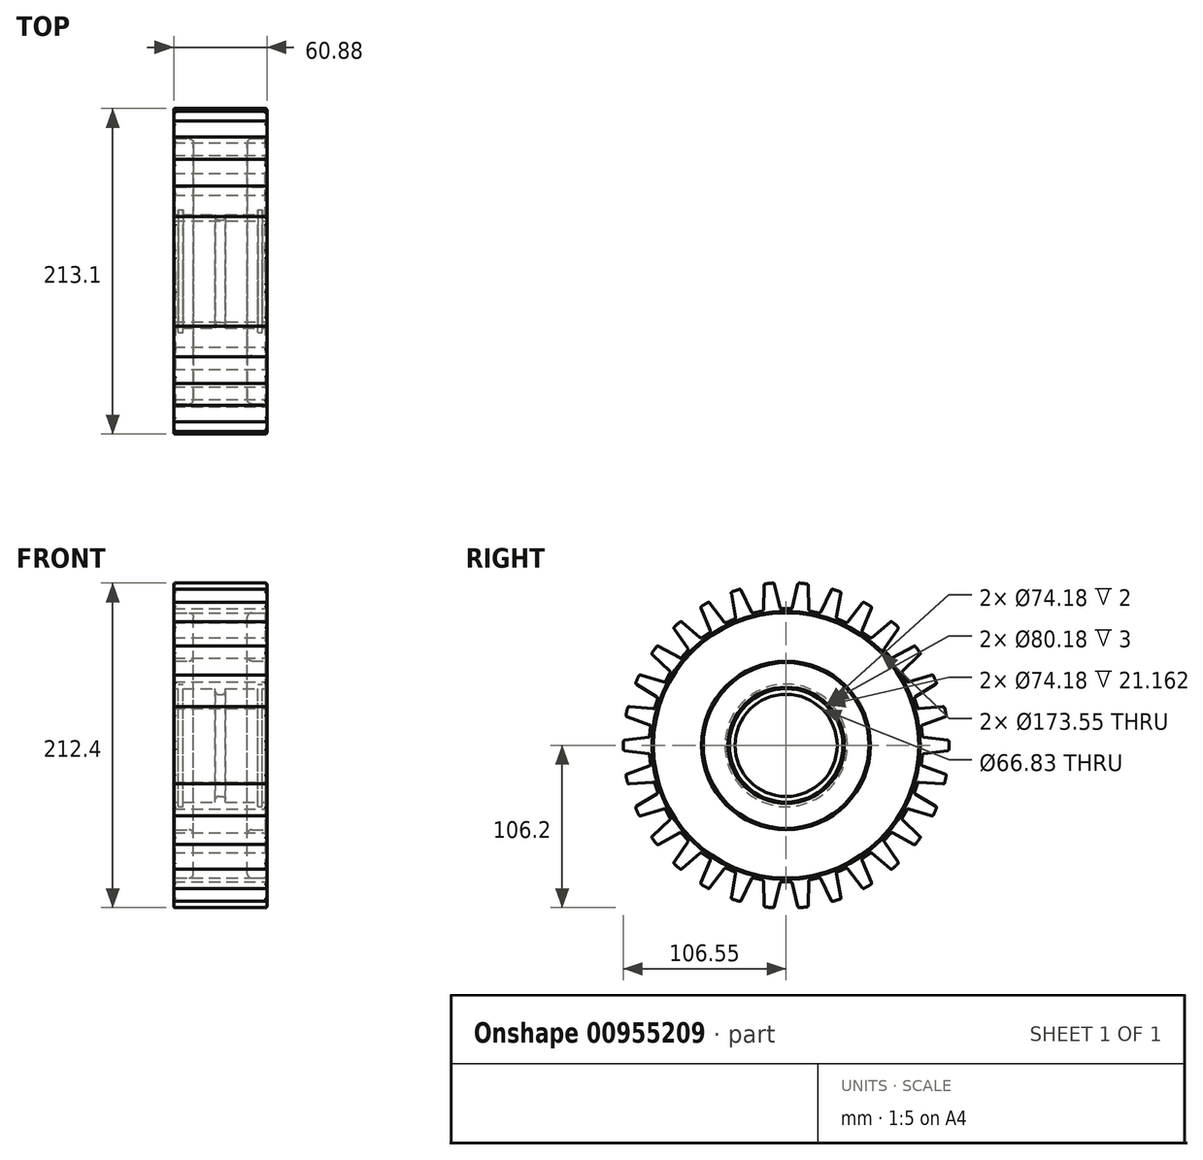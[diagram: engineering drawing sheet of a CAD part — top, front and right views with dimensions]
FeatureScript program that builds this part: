
annotation { "Feature Type Name" : "Feature", "Feature Type Description" : "" }
export const myFeature = defineFeature(function(context is Context, id is Id, definition is map)
    precondition{}
    {
        {
            var Q0;
            Q0=qCreatedBy(makeId("Front.planeOp"),FACE);
            var sketch = newSketch(context, id + "F0", { "sketchPlane" : qUnion([Q0])});
            skLineSegment(sketch, "E0", {"start": v(0, 106.55) * mm, "end": v(-30.44, 106.55) * mm});
            skLineSegment(sketch, "E1", {"start": v(-30.44, 106.55) * mm, "end": v(-30.44, 86.78) * mm});
            skLineSegment(sketch, "E2", {"start": v(-30.44, 37.1) * mm, "end": v(-27.44, 37.1) * mm});
            skLineSegment(sketch, "E3", {"start": v(-27.44, 37.1) * mm, "end": v(-27.44, 40.1) * mm});
            skLineSegment(sketch, "E4", {"start": v(-27.44, 40.1) * mm, "end": v(-24.44, 40.1) * mm});
            skLineSegment(sketch, "E5", {"start": v(-24.44, 40.1) * mm, "end": v(-24.44, 37.1) * mm});
            skLineSegment(sketch, "E6", {"start": v(-24.44, 37.1) * mm, "end": v(-3.28, 37.1) * mm});
            skLineSegment(sketch, "E7", {"start": v(-3.28, 37.1) * mm, "end": v(-3.28, 33.41) * mm});
            skLineSegment(sketch, "E8", {"start": v(-3.28, 33.41) * mm, "end": v(0, 33.41) * mm});
            skLineSegment(sketch, "E9", {"start": v(-30.44, 55.2) * mm, "end": v(-20.58, 55.2) * mm});
            skLineSegment(sketch, "E10", {"start": v(-17.58, 58.2) * mm, "end": v(-17.58, 83.78) * mm});
            skLineSegment(sketch, "E11", {"start": v(-20.58, 86.78) * mm, "end": v(-30.44, 86.78) * mm});
            skLineSegment(sketch, "E12.trimOffspring", {"start": v(-30.44, 55.2) * mm, "end": v(-30.44, 37.1) * mm});
            skPoint(sketch, "E13.visualSharp", {"position": v(-17.58, 86.78) * mm});
            skArc(sketch, "E13.filletArc", {"start": v(-17.58, 83.78) * mm, "mid": v(-18.46, 85.9) * mm, "end": v(-20.58, 86.78) * mm});
            skPoint(sketch, "E14.visualSharp", {"position": v(-17.58, 55.2) * mm});
            skArc(sketch, "E14.filletArc", {"start": v(-20.58, 55.2) * mm, "mid": v(-18.46, 56.08) * mm, "end": v(-17.58, 58.2) * mm});
            skLineSegment(sketch, "E15.MirrorCS", {"start": v(0, 106.55) * mm, "end": v(30.44, 106.55) * mm});
            skLineSegment(sketch, "E16.MirrorCS", {"start": v(30.44, 106.55) * mm, "end": v(30.44, 86.78) * mm});
            skLineSegment(sketch, "E17.MirrorCS", {"start": v(20.58, 86.78) * mm, "end": v(30.44, 86.78) * mm});
            skArc(sketch, "E18.MirrorCS", {"start": v(17.58, 83.78) * mm, "mid": v(18.46, 85.9) * mm, "end": v(20.58, 86.78) * mm});
            skLineSegment(sketch, "E19.MirrorCS", {"start": v(17.58, 58.2) * mm, "end": v(17.58, 83.78) * mm});
            skArc(sketch, "E20.MirrorCS", {"start": v(20.58, 55.2) * mm, "mid": v(18.46, 56.08) * mm, "end": v(17.58, 58.2) * mm});
            skLineSegment(sketch, "E21.MirrorCS", {"start": v(30.44, 55.2) * mm, "end": v(20.58, 55.2) * mm});
            skLineSegment(sketch, "E22.MirrorCS", {"start": v(30.44, 55.2) * mm, "end": v(30.44, 37.1) * mm});
            skLineSegment(sketch, "E23.MirrorCS", {"start": v(30.44, 37.1) * mm, "end": v(27.44, 37.1) * mm});
            skLineSegment(sketch, "E24.MirrorCS", {"start": v(27.44, 40.1) * mm, "end": v(24.44, 40.1) * mm});
            skLineSegment(sketch, "E25.MirrorCS", {"start": v(24.44, 40.1) * mm, "end": v(24.44, 37.1) * mm});
            skLineSegment(sketch, "E26.MirrorCS", {"start": v(24.44, 37.1) * mm, "end": v(3.28, 37.1) * mm});
            skLineSegment(sketch, "E27.MirrorCS", {"start": v(3.28, 37.1) * mm, "end": v(3.28, 33.41) * mm});
            skLineSegment(sketch, "E28.MirrorCS", {"start": v(3.28, 33.41) * mm, "end": v(0, 33.41) * mm});
            skLineSegment(sketch, "E29.MirrorCS", {"start": v(27.44, 37.1) * mm, "end": v(27.44, 40.1) * mm});
            skLineSegment(sketch, "E30", {"start": v(0, 0) * mm, "end": v(-35.69, 0) * mm, "construction": true});
            skSolve(sketch);
        }
        {
            var Q0;
            Q0=makeQuery(id+"F0.imprint","IMPRINT",FACE,{"disambiguationData":[TD([[makeQuery(id+"F0.imprint","IMPRINT",EDGE,{"derivedFrom":sQuery(id+"F0.wireOp",EDGE,"E0")}),1.0]])]});
            var Q1;
            Q1=sQuery(id+"F0.wireOp",EDGE,"E30");
            revolve(context, id + "F1", {"surfaceOperationType" : NewSurfaceOperationType.NEW, "entities" : qUnion([Q0]), "axis" : qUnion([Q1]), "revolveType" : RevolveType.FULL});
        }
        {
            var Q0;
            Q0=qCreatedBy(makeId("Right.planeOp"),FACE);
            var sketch = newSketch(context, id + "F2", { "sketchPlane" : qUnion([Q0])});
            skLineSegment(sketch, "E31", {"start": v(0, 0) * mm, "end": v(0, 103.53) * mm});
            skLineSegment(sketch, "E32", {"start": v(4.04, 90.14) * mm, "end": v(8.11, 107.16) * mm});
            skLineSegment(sketch, "E33.MirrorCS", {"start": v(-4.04, 90.14) * mm, "end": v(-8.11, 107.16) * mm});
            skLineSegment(sketch, "E34", {"start": v(-3.06, 89.37) * mm, "end": v(3.06, 89.37) * mm});
            skLineSegment(sketch, "E35", {"start": v(8.11, 107.16) * mm, "end": v(-8.11, 107.16) * mm});
            skPoint(sketch, "E36.visualSharp", {"position": v(-3.85, 89.37) * mm});
            skArc(sketch, "E36.filletArc", {"start": v(-4.04, 90.14) * mm, "mid": v(-3.68, 89.58) * mm, "end": v(-3.06, 89.37) * mm});
            skPoint(sketch, "E37.visualSharp", {"position": v(3.85, 89.37) * mm});
            skArc(sketch, "E37.filletArc", {"start": v(3.06, 89.37) * mm, "mid": v(3.68, 89.58) * mm, "end": v(4.04, 90.14) * mm});
            skSolve(sketch);
        }
        {
            var Q0;
            Q0=makeQuery(id+"F2.imprint","IMPRINT",FACE,{"disambiguationData":[TD([[makeQuery(id+"F2.imprint","IMPRINT",EDGE,{"derivedFrom":sQuery(id+"F2.wireOp",EDGE,"E32")}),1.0]])]});
            extrude(context, id + "F3", {"entities" : qUnion([Q0]), "operationType" : NewBodyOperationType.REMOVE, "endBound" : BoundingType.SYMMETRIC, "oppositeDirection" : true, "depth" : 70 * mm, "offsetDistance" : 25 * mm});
        }
        {
            var Q0;
            Q0=makeQuery(id+"F3.boolean.opBoolean","COPY",FACE,{"derivedFrom":makeQuery(id+"F3.opExtrude","SWEPT_FACE",FACE,{"disambiguationData":[OSD([sQuery(id+"F2.wireOp",EDGE,"E32")])]})});
            var Q1;
            Q1=makeQuery(id+"F3.boolean.opBoolean","COPY",FACE,{"derivedFrom":makeQuery(id+"F3.opExtrude","SWEPT_FACE",FACE,{"disambiguationData":[OSD([sQuery(id+"F2.wireOp",EDGE,"E37.filletArc")])]})});
            var Q2;
            Q2=makeQuery(id+"F3.boolean.opBoolean","COPY",FACE,{"derivedFrom":makeQuery(id+"F3.opExtrude","SWEPT_FACE",FACE,{"disambiguationData":[OSD([sQuery(id+"F2.wireOp",EDGE,"E34")])]})});
            var Q3;
            Q3=makeQuery(id+"F3.boolean.opBoolean","COPY",FACE,{"derivedFrom":makeQuery(id+"F3.opExtrude","SWEPT_FACE",FACE,{"disambiguationData":[OSD([sQuery(id+"F2.wireOp",EDGE,"E36.filletArc")])]})});
            var Q4;
            Q4=makeQuery(id+"F3.boolean.opBoolean","COPY",FACE,{"derivedFrom":makeQuery(id+"F3.opExtrude","SWEPT_FACE",FACE,{"disambiguationData":[OSD([sQuery(id+"F2.wireOp",EDGE,"E33.MirrorCS")])]})});
            var Q5;
            Q5=sQuery(id+"F0.wireOp",EDGE,"E30");
            circularPattern(context, id + "F4", {"patternType" : PatternType.FACE, "faces" : qUnion([Q0, Q1, Q2, Q3, Q4]), "axis" : qUnion([Q5]), "angle" : 360 * degree, "instanceCount" : 30, "equalSpace" : true});
        }
        {
            var Q0;
            Q0=makeQuery(id+"F1.opRevolve","SWEPT_EDGE",EDGE,{"disambiguationData":[OSD([sQuery(id+"F0.wireOp",EDGE,"E1"),sQuery(id+"F0.wireOp",EDGE,"E11")])]});
            var Q1;
            Q1=makeQuery(id+"F1.opRevolve","SWEPT_EDGE",EDGE,{"disambiguationData":[OSD([sQuery(id+"F0.wireOp",EDGE,"E9"),sQuery(id+"F0.wireOp",EDGE,"E12.trimOffspring")])]});
            var Q2;
            Q2=makeQuery(id+"F1.opRevolve","SWEPT_EDGE",EDGE,{"disambiguationData":[OSD([sQuery(id+"F0.wireOp",EDGE,"E2"),sQuery(id+"F0.wireOp",EDGE,"E12.trimOffspring")])]});
            var Q3;
            Q3=makeQuery(id+"F1.opRevolve","SWEPT_EDGE",EDGE,{"disambiguationData":[OSD([sQuery(id+"F0.wireOp",EDGE,"E16.MirrorCS"),sQuery(id+"F0.wireOp",EDGE,"E17.MirrorCS")])]});
            var Q4;
            Q4=makeQuery(id+"F1.opRevolve","SWEPT_EDGE",EDGE,{"disambiguationData":[OSD([sQuery(id+"F0.wireOp",EDGE,"E21.MirrorCS"),sQuery(id+"F0.wireOp",EDGE,"E22.MirrorCS")])]});
            var Q5;
            Q5=makeQuery(id+"F1.opRevolve","SWEPT_EDGE",EDGE,{"disambiguationData":[OSD([sQuery(id+"F0.wireOp",EDGE,"E22.MirrorCS"),sQuery(id+"F0.wireOp",EDGE,"E23.MirrorCS")])]});
            chamfer(context, id + "F5", {"entities" : qUnion([Q0, Q1, Q2, Q3, Q4, Q5]), "width" : 1 * mm, "tangentPropagation" : true});
        }
        {
            var Q0;
            Q0=makeQuery(id+"F4.opPattern","COPY",EDGE,{"derivedFrom":makeQuery(id+"F3.boolean.opBoolean","INTERSECT",EDGE,{"derivedFrom":[makeQuery(id+"F1.opRevolve","SWEPT_FACE",FACE,{"disambiguationData":[OSD([sQuery(id+"F0.wireOp",EDGE,"E0"),sQuery(id+"F0.wireOp",EDGE,"E15.MirrorCS")])]}),makeQuery(id+"F3.opExtrude","SWEPT_FACE",FACE,{"disambiguationData":[OSD([sQuery(id+"F2.wireOp",EDGE,"E33.MirrorCS")])]})]}),"instanceName":"3"});
            var Q1;
            Q1=makeQuery(id+"F4.opPattern","COPY",EDGE,{"derivedFrom":makeQuery(id+"F3.boolean.opBoolean","INTERSECT",EDGE,{"derivedFrom":[makeQuery(id+"F1.opRevolve","SWEPT_FACE",FACE,{"disambiguationData":[OSD([sQuery(id+"F0.wireOp",EDGE,"E0"),sQuery(id+"F0.wireOp",EDGE,"E15.MirrorCS")])]}),makeQuery(id+"F3.opExtrude","SWEPT_FACE",FACE,{"disambiguationData":[OSD([sQuery(id+"F2.wireOp",EDGE,"E32")])]})]}),"instanceName":"2"});
            var Q2;
            Q2=makeQuery(id+"F4.opPattern","COPY",EDGE,{"derivedFrom":makeQuery(id+"F3.boolean.opBoolean","INTERSECT",EDGE,{"derivedFrom":[makeQuery(id+"F1.opRevolve","SWEPT_FACE",FACE,{"disambiguationData":[OSD([sQuery(id+"F0.wireOp",EDGE,"E0"),sQuery(id+"F0.wireOp",EDGE,"E15.MirrorCS")])]}),makeQuery(id+"F3.opExtrude","SWEPT_FACE",FACE,{"disambiguationData":[OSD([sQuery(id+"F2.wireOp",EDGE,"E32")])]})]}),"instanceName":"3"});
            var Q3;
            Q3=makeQuery(id+"F4.opPattern","SPLIT",EDGE,{"disambiguationData":[OD(3.0)],"derivedFrom":makeQuery(id+"F1.opRevolve","SWEPT_EDGE",EDGE,{"disambiguationData":[OSD([sQuery(id+"F0.wireOp",EDGE,"E0"),sQuery(id+"F0.wireOp",EDGE,"E1")])]})});
            var Q4;
            Q4=makeQuery(id+"F4.opPattern","SPLIT",EDGE,{"disambiguationData":[OD(3.0)],"derivedFrom":makeQuery(id+"F1.opRevolve","SWEPT_EDGE",EDGE,{"disambiguationData":[OSD([sQuery(id+"F0.wireOp",EDGE,"E15.MirrorCS"),sQuery(id+"F0.wireOp",EDGE,"E16.MirrorCS")])]})});
            var Q5;
            Q5=makeQuery(id+"F4.opPattern","SPLIT",EDGE,{"disambiguationData":[OD(4.0)],"derivedFrom":makeQuery(id+"F1.opRevolve","SWEPT_EDGE",EDGE,{"disambiguationData":[OSD([sQuery(id+"F0.wireOp",EDGE,"E0"),sQuery(id+"F0.wireOp",EDGE,"E1")])]})});
            var Q6;
            Q6=makeQuery(id+"F4.opPattern","SPLIT",EDGE,{"disambiguationData":[OD(4.0)],"derivedFrom":makeQuery(id+"F1.opRevolve","SWEPT_EDGE",EDGE,{"disambiguationData":[OSD([sQuery(id+"F0.wireOp",EDGE,"E15.MirrorCS"),sQuery(id+"F0.wireOp",EDGE,"E16.MirrorCS")])]})});
            var Q7;
            Q7=makeQuery(id+"F4.opPattern","COPY",EDGE,{"derivedFrom":makeQuery(id+"F3.boolean.opBoolean","INTERSECT",EDGE,{"derivedFrom":[makeQuery(id+"F1.opRevolve","SWEPT_FACE",FACE,{"disambiguationData":[OSD([sQuery(id+"F0.wireOp",EDGE,"E0"),sQuery(id+"F0.wireOp",EDGE,"E15.MirrorCS")])]}),makeQuery(id+"F3.opExtrude","SWEPT_FACE",FACE,{"disambiguationData":[OSD([sQuery(id+"F2.wireOp",EDGE,"E33.MirrorCS")])]})]}),"instanceName":"4"});
            var Q8;
            Q8=makeQuery(id+"F4.opPattern","SPLIT",EDGE,{"disambiguationData":[OD(5.0)],"derivedFrom":makeQuery(id+"F1.opRevolve","SWEPT_EDGE",EDGE,{"disambiguationData":[OSD([sQuery(id+"F0.wireOp",EDGE,"E0"),sQuery(id+"F0.wireOp",EDGE,"E1")])]})});
            var Q9;
            Q9=makeQuery(id+"F4.opPattern","COPY",EDGE,{"derivedFrom":makeQuery(id+"F3.boolean.opBoolean","INTERSECT",EDGE,{"derivedFrom":[makeQuery(id+"F1.opRevolve","SWEPT_FACE",FACE,{"disambiguationData":[OSD([sQuery(id+"F0.wireOp",EDGE,"E0"),sQuery(id+"F0.wireOp",EDGE,"E15.MirrorCS")])]}),makeQuery(id+"F3.opExtrude","SWEPT_FACE",FACE,{"disambiguationData":[OSD([sQuery(id+"F2.wireOp",EDGE,"E32")])]})]}),"instanceName":"4"});
            var Q10;
            Q10=makeQuery(id+"F4.opPattern","SPLIT",EDGE,{"disambiguationData":[OD(5.0)],"derivedFrom":makeQuery(id+"F1.opRevolve","SWEPT_EDGE",EDGE,{"disambiguationData":[OSD([sQuery(id+"F0.wireOp",EDGE,"E15.MirrorCS"),sQuery(id+"F0.wireOp",EDGE,"E16.MirrorCS")])]})});
            var Q11;
            Q11=makeQuery(id+"F4.opPattern","COPY",EDGE,{"derivedFrom":makeQuery(id+"F3.boolean.opBoolean","INTERSECT",EDGE,{"derivedFrom":[makeQuery(id+"F1.opRevolve","SWEPT_FACE",FACE,{"disambiguationData":[OSD([sQuery(id+"F0.wireOp",EDGE,"E0"),sQuery(id+"F0.wireOp",EDGE,"E15.MirrorCS")])]}),makeQuery(id+"F3.opExtrude","SWEPT_FACE",FACE,{"disambiguationData":[OSD([sQuery(id+"F2.wireOp",EDGE,"E33.MirrorCS")])]})]}),"instanceName":"5"});
            var Q12;
            Q12=makeQuery(id+"F4.opPattern","SPLIT",EDGE,{"disambiguationData":[OD(6.0)],"derivedFrom":makeQuery(id+"F1.opRevolve","SWEPT_EDGE",EDGE,{"disambiguationData":[OSD([sQuery(id+"F0.wireOp",EDGE,"E0"),sQuery(id+"F0.wireOp",EDGE,"E1")])]})});
            var Q13;
            Q13=makeQuery(id+"F4.opPattern","COPY",EDGE,{"derivedFrom":makeQuery(id+"F3.boolean.opBoolean","INTERSECT",EDGE,{"derivedFrom":[makeQuery(id+"F1.opRevolve","SWEPT_FACE",FACE,{"disambiguationData":[OSD([sQuery(id+"F0.wireOp",EDGE,"E0"),sQuery(id+"F0.wireOp",EDGE,"E15.MirrorCS")])]}),makeQuery(id+"F3.opExtrude","SWEPT_FACE",FACE,{"disambiguationData":[OSD([sQuery(id+"F2.wireOp",EDGE,"E32")])]})]}),"instanceName":"5"});
            var Q14;
            Q14=makeQuery(id+"F4.opPattern","SPLIT",FACE,{"disambiguationData":[OD(6.0)],"derivedFrom":makeQuery(id+"F1.opRevolve","SWEPT_FACE",FACE,{"disambiguationData":[OSD([sQuery(id+"F0.wireOp",EDGE,"E0"),sQuery(id+"F0.wireOp",EDGE,"E15.MirrorCS")])]})});
            var Q15;
            Q15=makeQuery(id+"F4.opPattern","SPLIT",FACE,{"disambiguationData":[OD(7.0)],"derivedFrom":makeQuery(id+"F1.opRevolve","SWEPT_FACE",FACE,{"disambiguationData":[OSD([sQuery(id+"F0.wireOp",EDGE,"E0"),sQuery(id+"F0.wireOp",EDGE,"E15.MirrorCS")])]})});
            var Q16;
            Q16=makeQuery(id+"F4.opPattern","SPLIT",FACE,{"disambiguationData":[OD(8.0)],"derivedFrom":makeQuery(id+"F1.opRevolve","SWEPT_FACE",FACE,{"disambiguationData":[OSD([sQuery(id+"F0.wireOp",EDGE,"E0"),sQuery(id+"F0.wireOp",EDGE,"E15.MirrorCS")])]})});
            var Q17;
            Q17=makeQuery(id+"F4.opPattern","SPLIT",FACE,{"disambiguationData":[OD(9.0)],"derivedFrom":makeQuery(id+"F1.opRevolve","SWEPT_FACE",FACE,{"disambiguationData":[OSD([sQuery(id+"F0.wireOp",EDGE,"E0"),sQuery(id+"F0.wireOp",EDGE,"E15.MirrorCS")])]})});
            var Q18;
            Q18=makeQuery(id+"F4.opPattern","SPLIT",FACE,{"disambiguationData":[OD(10.0)],"derivedFrom":makeQuery(id+"F1.opRevolve","SWEPT_FACE",FACE,{"disambiguationData":[OSD([sQuery(id+"F0.wireOp",EDGE,"E0"),sQuery(id+"F0.wireOp",EDGE,"E15.MirrorCS")])]})});
            var Q19;
            Q19=makeQuery(id+"F4.opPattern","SPLIT",FACE,{"disambiguationData":[OD(11.0)],"derivedFrom":makeQuery(id+"F1.opRevolve","SWEPT_FACE",FACE,{"disambiguationData":[OSD([sQuery(id+"F0.wireOp",EDGE,"E0"),sQuery(id+"F0.wireOp",EDGE,"E15.MirrorCS")])]})});
            var Q20;
            Q20=makeQuery(id+"F4.opPattern","SPLIT",FACE,{"disambiguationData":[OD(12.0)],"derivedFrom":makeQuery(id+"F1.opRevolve","SWEPT_FACE",FACE,{"disambiguationData":[OSD([sQuery(id+"F0.wireOp",EDGE,"E0"),sQuery(id+"F0.wireOp",EDGE,"E15.MirrorCS")])]})});
            var Q21;
            Q21=makeQuery(id+"F4.opPattern","SPLIT",FACE,{"disambiguationData":[OD(13.0)],"derivedFrom":makeQuery(id+"F1.opRevolve","SWEPT_FACE",FACE,{"disambiguationData":[OSD([sQuery(id+"F0.wireOp",EDGE,"E0"),sQuery(id+"F0.wireOp",EDGE,"E15.MirrorCS")])]})});
            var Q22;
            Q22=makeQuery(id+"F4.opPattern","SPLIT",FACE,{"disambiguationData":[OD(14.0)],"derivedFrom":makeQuery(id+"F1.opRevolve","SWEPT_FACE",FACE,{"disambiguationData":[OSD([sQuery(id+"F0.wireOp",EDGE,"E0"),sQuery(id+"F0.wireOp",EDGE,"E15.MirrorCS")])]})});
            var Q23;
            Q23=makeQuery(id+"F4.opPattern","SPLIT",FACE,{"disambiguationData":[OD(15.0)],"derivedFrom":makeQuery(id+"F1.opRevolve","SWEPT_FACE",FACE,{"disambiguationData":[OSD([sQuery(id+"F0.wireOp",EDGE,"E0"),sQuery(id+"F0.wireOp",EDGE,"E15.MirrorCS")])]})});
            var Q24;
            Q24=makeQuery(id+"F4.opPattern","SPLIT",FACE,{"disambiguationData":[OD(16.0)],"derivedFrom":makeQuery(id+"F1.opRevolve","SWEPT_FACE",FACE,{"disambiguationData":[OSD([sQuery(id+"F0.wireOp",EDGE,"E0"),sQuery(id+"F0.wireOp",EDGE,"E15.MirrorCS")])]})});
            var Q25;
            Q25=makeQuery(id+"F4.opPattern","SPLIT",FACE,{"disambiguationData":[OD(17.0)],"derivedFrom":makeQuery(id+"F1.opRevolve","SWEPT_FACE",FACE,{"disambiguationData":[OSD([sQuery(id+"F0.wireOp",EDGE,"E0"),sQuery(id+"F0.wireOp",EDGE,"E15.MirrorCS")])]})});
            var Q26;
            Q26=makeQuery(id+"F4.opPattern","SPLIT",FACE,{"disambiguationData":[OD(18.0)],"derivedFrom":makeQuery(id+"F1.opRevolve","SWEPT_FACE",FACE,{"disambiguationData":[OSD([sQuery(id+"F0.wireOp",EDGE,"E0"),sQuery(id+"F0.wireOp",EDGE,"E15.MirrorCS")])]})});
            var Q27;
            Q27=makeQuery(id+"F4.opPattern","SPLIT",FACE,{"disambiguationData":[OD(19.0)],"derivedFrom":makeQuery(id+"F1.opRevolve","SWEPT_FACE",FACE,{"disambiguationData":[OSD([sQuery(id+"F0.wireOp",EDGE,"E0"),sQuery(id+"F0.wireOp",EDGE,"E15.MirrorCS")])]})});
            var Q28;
            Q28=makeQuery(id+"F4.opPattern","SPLIT",FACE,{"disambiguationData":[OD(20.0)],"derivedFrom":makeQuery(id+"F1.opRevolve","SWEPT_FACE",FACE,{"disambiguationData":[OSD([sQuery(id+"F0.wireOp",EDGE,"E0"),sQuery(id+"F0.wireOp",EDGE,"E15.MirrorCS")])]})});
            var Q29;
            Q29=makeQuery(id+"F4.opPattern","SPLIT",FACE,{"disambiguationData":[OD(21.0)],"derivedFrom":makeQuery(id+"F1.opRevolve","SWEPT_FACE",FACE,{"disambiguationData":[OSD([sQuery(id+"F0.wireOp",EDGE,"E0"),sQuery(id+"F0.wireOp",EDGE,"E15.MirrorCS")])]})});
            var Q30;
            Q30=makeQuery(id+"F4.opPattern","SPLIT",FACE,{"disambiguationData":[OD(22.0)],"derivedFrom":makeQuery(id+"F1.opRevolve","SWEPT_FACE",FACE,{"disambiguationData":[OSD([sQuery(id+"F0.wireOp",EDGE,"E0"),sQuery(id+"F0.wireOp",EDGE,"E15.MirrorCS")])]})});
            var Q31;
            Q31=makeQuery(id+"F4.opPattern","SPLIT",FACE,{"disambiguationData":[OD(2.0)],"derivedFrom":makeQuery(id+"F1.opRevolve","SWEPT_FACE",FACE,{"disambiguationData":[OSD([sQuery(id+"F0.wireOp",EDGE,"E0"),sQuery(id+"F0.wireOp",EDGE,"E15.MirrorCS")])]})});
            var Q32;
            Q32=makeQuery(id+"F4.opPattern","SPLIT",FACE,{"disambiguationData":[OD(0.0)],"derivedFrom":makeQuery(id+"F1.opRevolve","SWEPT_FACE",FACE,{"disambiguationData":[OSD([sQuery(id+"F0.wireOp",EDGE,"E0"),sQuery(id+"F0.wireOp",EDGE,"E15.MirrorCS")])]})});
            var Q33;
            Q33=makeQuery(id+"F4.opPattern","SPLIT",FACE,{"disambiguationData":[OD(1.0)],"derivedFrom":makeQuery(id+"F1.opRevolve","SWEPT_FACE",FACE,{"disambiguationData":[OSD([sQuery(id+"F0.wireOp",EDGE,"E0"),sQuery(id+"F0.wireOp",EDGE,"E15.MirrorCS")])]})});
            var Q34;
            Q34=makeQuery(id+"F4.opPattern","SPLIT",FACE,{"disambiguationData":[OD(29.0)],"derivedFrom":makeQuery(id+"F1.opRevolve","SWEPT_FACE",FACE,{"disambiguationData":[OSD([sQuery(id+"F0.wireOp",EDGE,"E0"),sQuery(id+"F0.wireOp",EDGE,"E15.MirrorCS")])]})});
            var Q35;
            Q35=makeQuery(id+"F4.opPattern","SPLIT",FACE,{"disambiguationData":[OD(28.0)],"derivedFrom":makeQuery(id+"F1.opRevolve","SWEPT_FACE",FACE,{"disambiguationData":[OSD([sQuery(id+"F0.wireOp",EDGE,"E0"),sQuery(id+"F0.wireOp",EDGE,"E15.MirrorCS")])]})});
            var Q36;
            Q36=makeQuery(id+"F4.opPattern","SPLIT",FACE,{"disambiguationData":[OD(27.0)],"derivedFrom":makeQuery(id+"F1.opRevolve","SWEPT_FACE",FACE,{"disambiguationData":[OSD([sQuery(id+"F0.wireOp",EDGE,"E0"),sQuery(id+"F0.wireOp",EDGE,"E15.MirrorCS")])]})});
            var Q37;
            Q37=makeQuery(id+"F4.opPattern","SPLIT",FACE,{"disambiguationData":[OD(26.0)],"derivedFrom":makeQuery(id+"F1.opRevolve","SWEPT_FACE",FACE,{"disambiguationData":[OSD([sQuery(id+"F0.wireOp",EDGE,"E0"),sQuery(id+"F0.wireOp",EDGE,"E15.MirrorCS")])]})});
            var Q38;
            Q38=makeQuery(id+"F4.opPattern","SPLIT",FACE,{"disambiguationData":[OD(25.0)],"derivedFrom":makeQuery(id+"F1.opRevolve","SWEPT_FACE",FACE,{"disambiguationData":[OSD([sQuery(id+"F0.wireOp",EDGE,"E0"),sQuery(id+"F0.wireOp",EDGE,"E15.MirrorCS")])]})});
            var Q39;
            Q39=makeQuery(id+"F4.opPattern","SPLIT",FACE,{"disambiguationData":[OD(24.0)],"derivedFrom":makeQuery(id+"F1.opRevolve","SWEPT_FACE",FACE,{"disambiguationData":[OSD([sQuery(id+"F0.wireOp",EDGE,"E0"),sQuery(id+"F0.wireOp",EDGE,"E15.MirrorCS")])]})});
            var Q40;
            Q40=makeQuery(id+"F4.opPattern","SPLIT",FACE,{"disambiguationData":[OD(23.0)],"derivedFrom":makeQuery(id+"F1.opRevolve","SWEPT_FACE",FACE,{"disambiguationData":[OSD([sQuery(id+"F0.wireOp",EDGE,"E0"),sQuery(id+"F0.wireOp",EDGE,"E15.MirrorCS")])]})});
            fillet(context, id + "F6", {"entities" : qUnion([Q0, Q1, Q2, Q3, Q4, Q5, Q6, Q7, Q8, Q9, Q10, Q11, Q12, Q13, Q14, Q15, Q16, Q17, Q18, Q19, Q20, Q21, Q22, Q23, Q24, Q25, Q26, Q27, Q28, Q29, Q30, Q31, Q32, Q33, Q34, Q35, Q36, Q37, Q38, Q39, Q40]), "radius" : 1 * mm, "tangentPropagation" : true, "allowEdgeOverflow" : false});
        }
        {
            var Q0;
            Q0=makeQuery(id+"F1.opRevolve","SWEPT_EDGE",EDGE,{"disambiguationData":[OSD([sQuery(id+"F0.wireOp",EDGE,"E27.MirrorCS"),sQuery(id+"F0.wireOp",EDGE,"E28.MirrorCS")])]});
            var Q1;
            Q1=makeQuery(id+"F1.opRevolve","SWEPT_EDGE",EDGE,{"disambiguationData":[OSD([sQuery(id+"F0.wireOp",EDGE,"E7"),sQuery(id+"F0.wireOp",EDGE,"E8")])]});
            fillet(context, id + "F7", {"entities" : qUnion([Q0, Q1]), "radius" : 2 * mm, "tangentPropagation" : true, "allowEdgeOverflow" : false});
        }
    });
